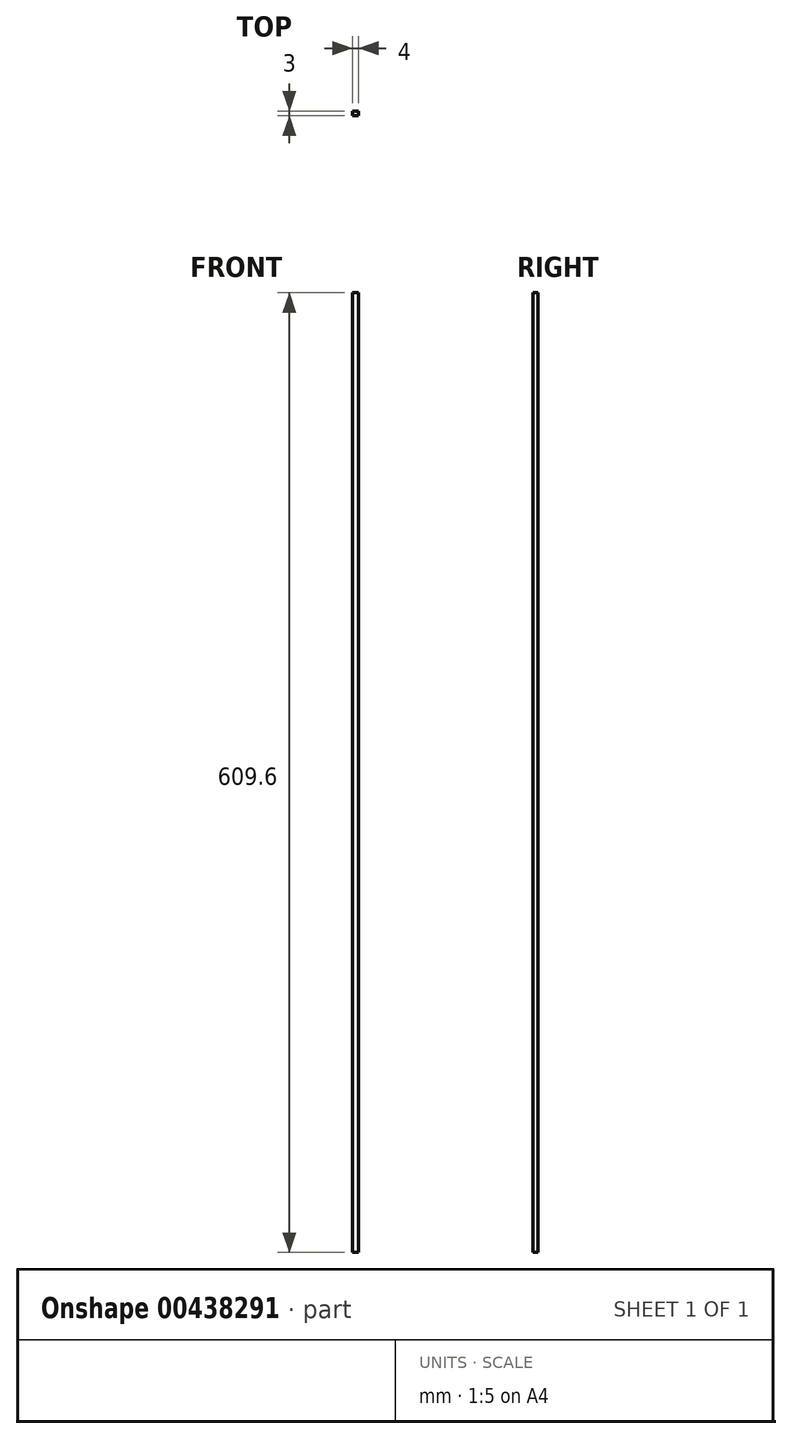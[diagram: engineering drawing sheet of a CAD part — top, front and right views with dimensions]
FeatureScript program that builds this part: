
annotation { "Feature Type Name" : "Feature", "Feature Type Description" : "" }
export const myFeature = defineFeature(function(context is Context, id is Id, definition is map)
    precondition{}
    {
        {
            var Q0;
            Q0=qCreatedBy(makeId("Front.planeOp"),FACE);
            var sketch = newSketch(context, id + "F0", { "sketchPlane" : qUnion([Q0])});
            skLineSegment(sketch, "E0.bottom", {"start": v(-4, 307.44) * mm, "end": v(0, 307.44) * mm});
            skLineSegment(sketch, "E0.top", {"start": v(-4, -302.16) * mm, "end": v(0, -302.16) * mm});
            skLineSegment(sketch, "E0.left", {"start": v(-4, 307.44) * mm, "end": v(-4, -302.16) * mm});
            skLineSegment(sketch, "E0.right", {"start": v(0, 307.44) * mm, "end": v(0, -302.16) * mm});
            skSolve(sketch);
        }
        {
            var Q0;
            Q0 = qSketchRegion(id + "F0", true);
            extrude(context, id + "F1", {"entities" : qUnion([Q0]), "depth" : 3 * mm});
        }
    });
